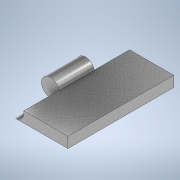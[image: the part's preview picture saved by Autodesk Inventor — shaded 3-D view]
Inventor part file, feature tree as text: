
AUTODESK INVENTOR PART (.ipt)
format: ipt  version: 2021 (Build 250183000, 183)  size: 122,880 bytes
history: native  units: mm
features: extrude x2, sketch x2, pattern_linear x1
ambient origin geometry x8: Origin, YZ Plane, XZ Plane, XY Plane, X Axis, Y Axis, Z Axis, Center Point
bodies: Solid1 (feature_tree)
feature tree (5):
  extrude  "Extrusion1"  Depth=3.0mm
  extrude  "Extrusion2"  Depth=30.0mm TaperAngle=0.0deg
  pattern_linear  "Rectangular Pattern1"  Spacing1=5.02mm  [1 undecoded]
  sketch  "Sketch1"  dims[d0=15.0mm d1=3.0mm]
  sketch  "Sketch2"  dims[d2=5.0mm d3=30.0mm d4=0.0mm d5=5.02mm d6=10.0mm d7=0.0mm d8=20.0mm d10=20.0mm d9=0.872665mm]
note: 1 required parameter value undecoded (feature->parameter linkage not recoverable at this tier; creation-order binding heuristic only, values carry confidence <= 0.55)
